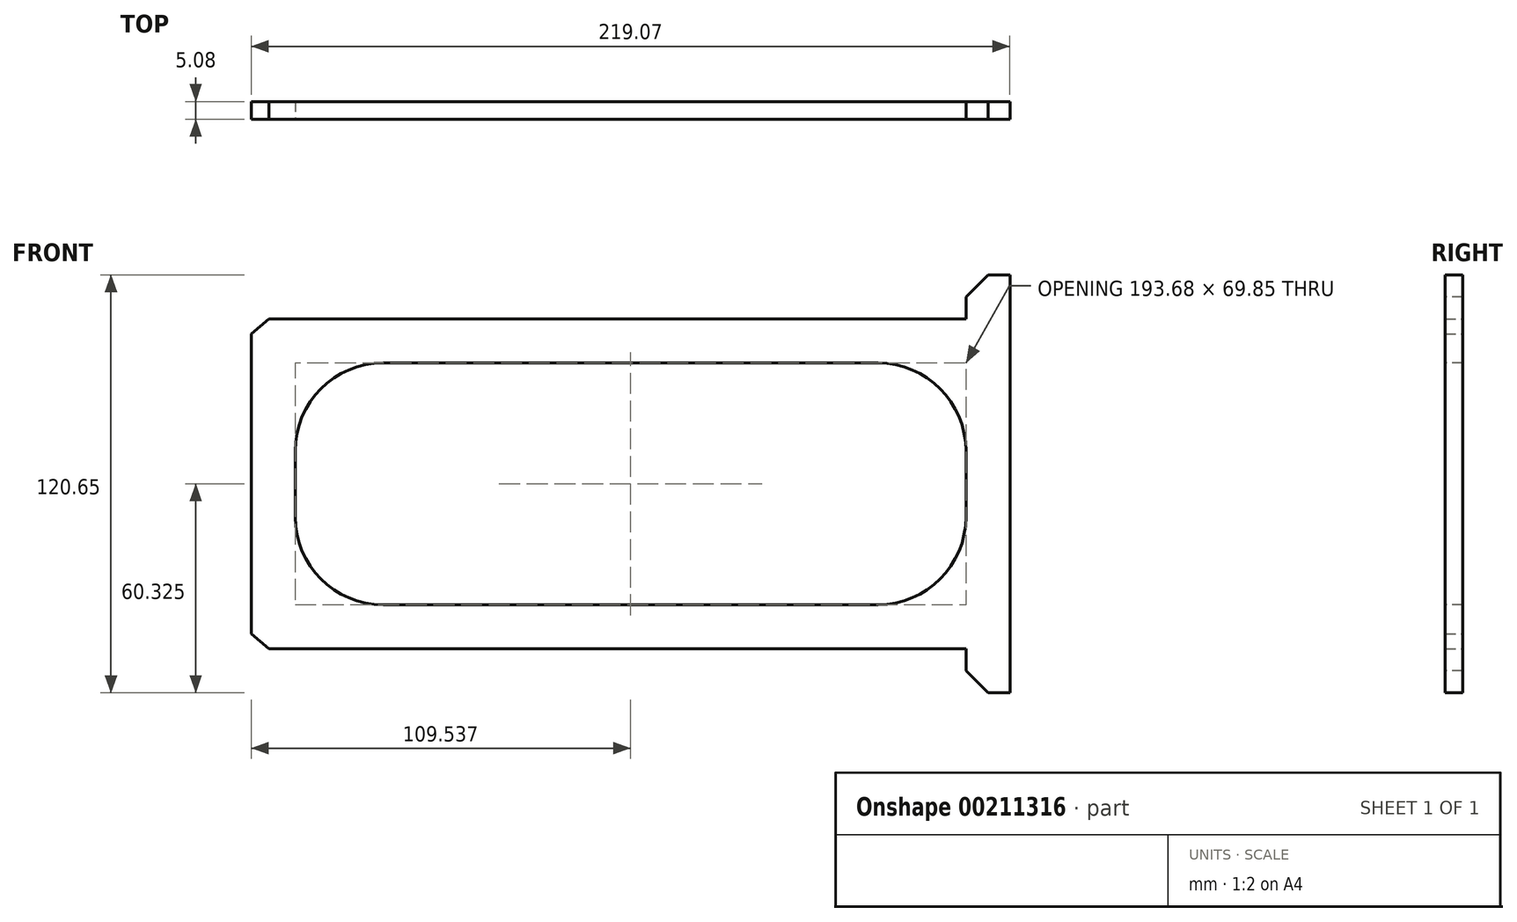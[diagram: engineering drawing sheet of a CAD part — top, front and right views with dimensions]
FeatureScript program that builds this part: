
annotation { "Feature Type Name" : "Feature", "Feature Type Description" : "" }
export const myFeature = defineFeature(function(context is Context, id is Id, definition is map)
    precondition{}
    {
        {
            var Q0;
            Q0=qCreatedBy(makeId("Front.planeOp"),FACE);
            var sketch = newSketch(context, id + "F0", { "sketchPlane" : qUnion([Q0])});
            skLineSegment(sketch, "E0.bottom", {"start": v(0, 0) * mm, "end": v(219.08, 0) * mm});
            skLineSegment(sketch, "E0.top", {"start": v(0, 95.25) * mm, "end": v(219.08, 95.25) * mm});
            skLineSegment(sketch, "E0.left", {"start": v(0, 0) * mm, "end": v(0, 95.25) * mm});
            skLineSegment(sketch, "E0.right", {"start": v(219.08, 0) * mm, "end": v(219.08, 95.25) * mm});
            skLineSegment(sketch, "E1", {"start": v(12.7, 101.6) * mm, "end": v(0, 90.94) * mm});
            skLineSegment(sketch, "E2", {"start": v(12.7, -6.35) * mm, "end": v(0, 4.3) * mm});
            skSolve(sketch);
        }
        {
            var Q0;
            {var subQ0=sQuery(id+"F0.wireOp",EDGE,"E0.right");Q0=makeQuery(id+"F0.imprint","IMPRINT",FACE,{"disambiguationData":[TD([[makeQuery(id+"F0.imprint","IMPRINT",EDGE,{"derivedFrom":subQ0}),1.0]])]});}
            extrude(context, id + "F1", {"entities" : qUnion([Q0]), "depth" : 5.08 * mm});
        }
        {
            var Q0;
            Q0=makeQuery(id+"F1.opExtrude","CAP_FACE",FACE,{"disambiguationData":[OSD([sQuery(id+"F0.wireOp",EDGE,"E0.bottom"),sQuery(id+"F0.wireOp",EDGE,"E0.top"),sQuery(id+"F0.wireOp",EDGE,"E0.left"),sQuery(id+"F0.wireOp",EDGE,"E0.right")])],"isStart":false});
            var sketch = newSketch(context, id + "F2", { "sketchPlane" : qUnion([Q0])});
            skLineSegment(sketch, "E3", {"start": v(12.7, 38.1) * mm, "end": v(12.7, 57.15) * mm});
            skLineSegment(sketch, "E4", {"start": v(38.1, 82.55) * mm, "end": v(180.97, 82.55) * mm});
            skLineSegment(sketch, "E5", {"start": v(206.38, 57.15) * mm, "end": v(206.38, 38.1) * mm});
            skLineSegment(sketch, "E6", {"start": v(180.98, 12.7) * mm, "end": v(38.1, 12.7) * mm});
            skPoint(sketch, "E7.visualSharp", {"position": v(12.7, 82.55) * mm});
            skArc(sketch, "E7.filletArc", {"start": v(38.1, 82.55) * mm, "mid": v(20.14, 75.11) * mm, "end": v(12.7, 57.15) * mm});
            skPoint(sketch, "E8.visualSharp", {"position": v(12.7, 12.7) * mm});
            skArc(sketch, "E8.filletArc", {"start": v(12.7, 38.1) * mm, "mid": v(20.14, 20.14) * mm, "end": v(38.1, 12.7) * mm});
            skPoint(sketch, "E9.visualSharp", {"position": v(206.38, 82.55) * mm});
            skArc(sketch, "E9.filletArc", {"start": v(206.38, 57.15) * mm, "mid": v(198.94, 75.11) * mm, "end": v(180.97, 82.55) * mm});
            skPoint(sketch, "E10.visualSharp", {"position": v(206.38, 12.7) * mm});
            skArc(sketch, "E10.filletArc", {"start": v(180.98, 12.7) * mm, "mid": v(198.94, 20.14) * mm, "end": v(206.38, 38.1) * mm});
            skSolve(sketch);
        }
        {
            var Q0;
            Q0=makeQuery(id+"F2.imprint","IMPRINT",FACE,{"disambiguationData":[TD([[makeQuery(id+"F2.imprint","IMPRINT",EDGE,{"derivedFrom":sQuery(id+"F2.wireOp",EDGE,"E3")}),-1.0]])]});
            extrude(context, id + "F3", {"entities" : qUnion([Q0]), "operationType" : NewBodyOperationType.REMOVE, "endBound" : BoundingType.THROUGH_ALL, "oppositeDirection" : true, "depth" : 25.4 * mm});
        }
        {
            var Q0;
            Q0=makeQuery(id+"F1.opExtrude","CAP_FACE",FACE,{"disambiguationData":[OSD([sQuery(id+"F0.wireOp",EDGE,"E0.bottom"),sQuery(id+"F0.wireOp",EDGE,"E0.top"),sQuery(id+"F0.wireOp",EDGE,"E0.left"),sQuery(id+"F0.wireOp",EDGE,"E0.right")])],"isStart":false});
            var sketch = newSketch(context, id + "F4", { "sketchPlane" : qUnion([Q0])});
            skLineSegment(sketch, "E11.bottom", {"start": v(219.08, -12.7) * mm, "end": v(206.38, -12.7) * mm});
            skLineSegment(sketch, "E11.top", {"start": v(219.08, 107.95) * mm, "end": v(206.38, 107.95) * mm});
            skLineSegment(sketch, "E11.left", {"start": v(219.08, -12.7) * mm, "end": v(219.08, 107.95) * mm});
            skLineSegment(sketch, "E11.right", {"start": v(206.38, -12.7) * mm, "end": v(206.38, 107.95) * mm});
            skLineSegment(sketch, "E12", {"start": v(206.38, 101.6) * mm, "end": v(212.73, 107.95) * mm});
            skLineSegment(sketch, "E13", {"start": v(206.38, -6.35) * mm, "end": v(212.73, -12.7) * mm});
            skSolve(sketch);
        }
        {
            var Q0;
            {var subQ0=sQuery(id+"F4.wireOp",EDGE,"E13");Q0=makeQuery(id+"F4.imprint","IMPRINT",FACE,{"disambiguationData":[TD([[makeQuery(id+"F4.imprint","IMPRINT",EDGE,{"derivedFrom":subQ0}),1.0]])]});}
            var Q1;
            {var subQ0=sQuery(id+"F4.wireOp",EDGE,"E12");Q1=makeQuery(id+"F4.imprint","IMPRINT",FACE,{"disambiguationData":[TD([[makeQuery(id+"F4.imprint","IMPRINT",EDGE,{"derivedFrom":subQ0}),-1.0]])]});}
            var Q2;
            {var subQ5=sQuery(id+"F4.wireOp",EDGE,"E11.left");var subQ6=makeQuery(id+"F1.opExtrude","CAP_EDGE",EDGE,{"disambiguationData":[OSD([sQuery(id+"F0.wireOp",EDGE,"E0.bottom")])],"isStart":false});var subQ7=makeQuery(id+"F4.imprint","INTERSECT",VERTEX,{"derivedFrom":[subQ6,subQ5]});Q2=makeQuery(id+"F4.imprint","IMPRINT",FACE,{"disambiguationData":[TD([[makeQuery(id+"F4.imprint","IMPRINT",EDGE,{"disambiguationData":[TD([[subQ7,-1.0]])],"derivedFrom":subQ5}),1.0]])]});}
            extrude(context, id + "F5", {"entities" : qUnion([Q0, Q1, Q2]), "operationType" : NewBodyOperationType.ADD, "oppositeDirection" : true, "depth" : 5.08 * mm});
        }
    });
